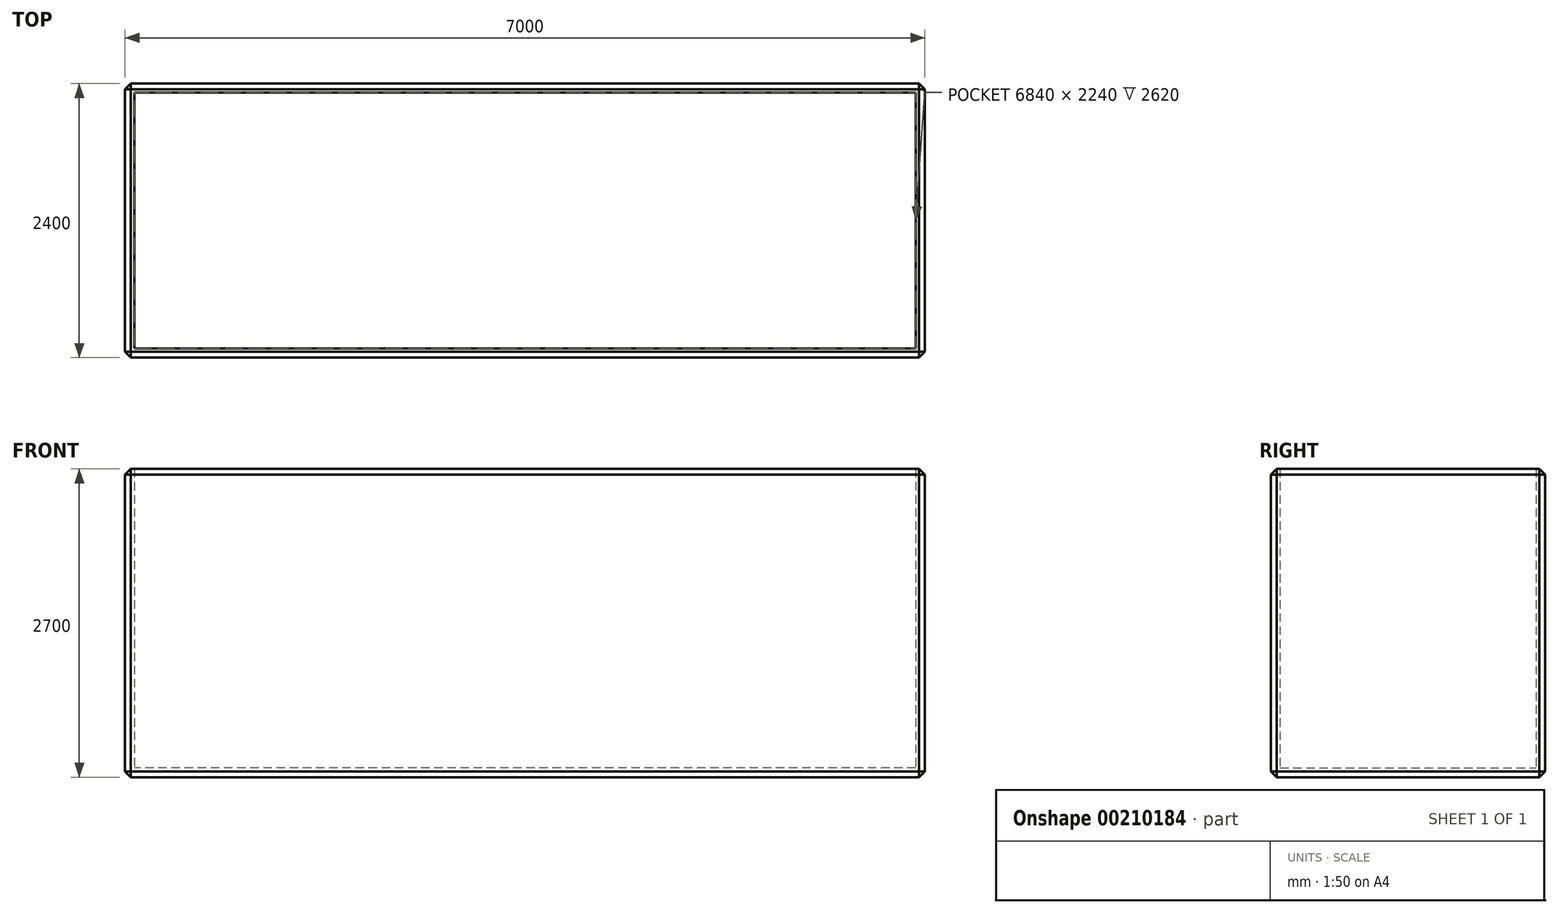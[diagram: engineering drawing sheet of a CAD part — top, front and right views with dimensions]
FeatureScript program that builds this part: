
annotation { "Feature Type Name" : "Feature", "Feature Type Description" : "" }
export const myFeature = defineFeature(function(context is Context, id is Id, definition is map)
    precondition{}
    {
        {
            var Q0;
            Q0=qCreatedBy(makeId("Top.planeOp"),FACE);
            var sketch = newSketch(context, id + "F0", { "sketchPlane" : qUnion([Q0])});
            skLineSegment(sketch, "E0.bottom", {"start": v(3500, -1200) * mm, "end": v(-3500, -1200) * mm});
            skLineSegment(sketch, "E0.top", {"start": v(3500, 1200) * mm, "end": v(-3500, 1200) * mm});
            skLineSegment(sketch, "E0.left", {"start": v(3500, -1200) * mm, "end": v(3500, 1200) * mm});
            skLineSegment(sketch, "E0.right", {"start": v(-3500, -1200) * mm, "end": v(-3500, 1200) * mm});
            skPoint(sketch, "E0.middle", {"position": v(0, 0) * mm});
            skSolve(sketch);
        }
        {
            var Q0;
            Q0 = qSketchRegion(id + "F0", true);
            extrude(context, id + "F1", {"entities" : qUnion([Q0]), "depth" : 2700 * mm});
        }
        {
            var Q0;
            Q0=makeQuery(id+"F1.opExtrude","CAP_FACE",FACE,{"disambiguationData":[OSD([sQuery(id+"F0.wireOp",EDGE,"E0.bottom"),sQuery(id+"F0.wireOp",EDGE,"E0.top"),sQuery(id+"F0.wireOp",EDGE,"E0.left"),sQuery(id+"F0.wireOp",EDGE,"E0.right")])],"isStart":false});
            shell(context, id + "F2", {"entities" : qUnion([Q0]), "thickness" : 80 * mm});
        }
        {
            var Q0;
            Q0=makeQuery(id+"F1.opExtrude","SWEPT_FACE",FACE,{"disambiguationData":[OSD([sQuery(id+"F0.wireOp",EDGE,"E0.bottom")])]});
            var Q1;
            Q1=makeQuery(id+"F1.opExtrude","SWEPT_FACE",FACE,{"disambiguationData":[OSD([sQuery(id+"F0.wireOp",EDGE,"E0.left")])]});
            var Q2;
            Q2=makeQuery(id+"F1.opExtrude","SWEPT_FACE",FACE,{"disambiguationData":[OSD([sQuery(id+"F0.wireOp",EDGE,"E0.top")])]});
            var Q3;
            Q3=makeQuery(id+"F1.opExtrude","SWEPT_FACE",FACE,{"disambiguationData":[OSD([sQuery(id+"F0.wireOp",EDGE,"E0.right")])]});
            chamfer(context, id + "F3", {"entities" : qUnion([Q0, Q1, Q2, Q3]), "width" : 50 * mm, "tangentPropagation" : true});
        }
    });
